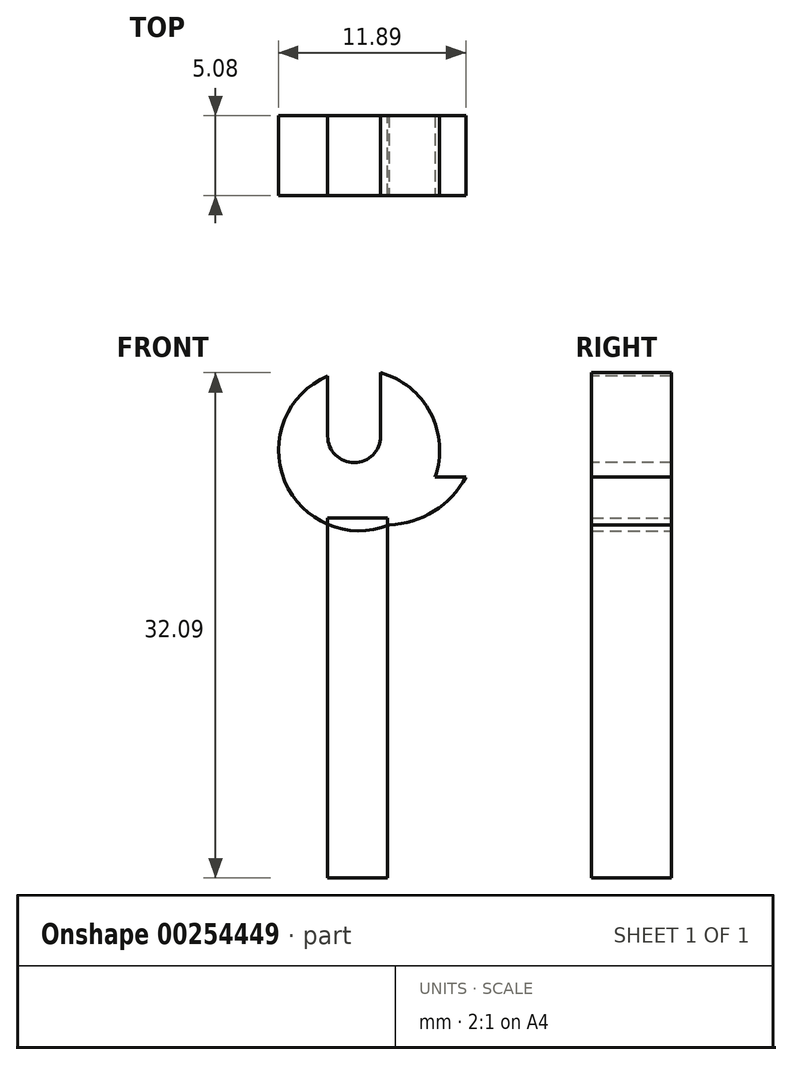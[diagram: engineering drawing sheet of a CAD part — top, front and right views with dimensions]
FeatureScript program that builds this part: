
annotation { "Feature Type Name" : "Feature", "Feature Type Description" : "" }
export const myFeature = defineFeature(function(context is Context, id is Id, definition is map)
    precondition{}
    {
        {
            var Q0;
            Q0=qCreatedBy(makeId("Front.planeOp"),FACE);
            var sketch = newSketch(context, id + "F0", { "sketchPlane" : qUnion([Q0])});
            skLineSegment(sketch, "E0.bottom", {"start": v(0, 0) * mm, "end": v(3.8, 0) * mm});
            skLineSegment(sketch, "E0.top", {"start": v(0, 22.86) * mm, "end": v(3.8, 22.86) * mm});
            skLineSegment(sketch, "E0.left", {"start": v(0, 0) * mm, "end": v(0, 22.86) * mm});
            skLineSegment(sketch, "E0.right", {"start": v(3.8, 0) * mm, "end": v(3.8, 22.86) * mm});
            skSolve(sketch);
        }
        {
            var Q0;
            Q0=qCreatedBy(makeId("Front.planeOp"),FACE);
            var sketch = newSketch(context, id + "F1", { "sketchPlane" : qUnion([Q0])});
            skCircle(sketch, "E1", {"center": v(2, 27.17) * mm, "radius": 5.11 * mm});
            skPoint(sketch, "E1.first.point", {"position": v(0, 22.46) * mm});
            skPoint(sketch, "E1.second.point", {"position": v(4, 22.46) * mm});
            skPoint(sketch, "E1.third.point", {"position": v(3.33, 32.1) * mm});
            skSolve(sketch);
        }
        {
            var Q0;
            Q0=makeQuery(id+"F1.imprint","IMPRINT",FACE,{"disambiguationData":[TD([[makeQuery(id+"F1.imprint","IMPRINT",EDGE,{"derivedFrom":sQuery(id+"F1.wireOp",EDGE,"E1")}),1.0]])]});
            var Q1;
            Q1=makeQuery(id+"F0.imprint","IMPRINT",FACE,{"disambiguationData":[TD([[makeQuery(id+"F0.imprint","IMPRINT",EDGE,{"derivedFrom":sQuery(id+"F0.wireOp",EDGE,"E0.bottom")}),1.0]])]});
            extrude(context, id + "F2", {"entities" : qUnion([Q0, Q1]), "depth" : 5.08 * mm});
        }
        {
            var Q0;
            Q0=makeQuery(id+"F2.opExtrude","CAP_FACE",FACE,{"disambiguationData":[OSD([sQuery(id+"F1.wireOp",EDGE,"E1")])],"isStart":false});
            var sketch = newSketch(context, id + "F3", { "sketchPlane" : qUnion([Q0])});
            skLineSegment(sketch, "E2", {"start": v(3.37, 32.1) * mm, "end": v(3.37, 28.06) * mm});
            skLineSegment(sketch, "E3", {"start": v(0, 31.87) * mm, "end": v(0, 28.06) * mm});
            skArc(sketch, "E4", {"start": v(0, 28.06) * mm, "mid": v(1.68, 26.37) * mm, "end": v(3.37, 28.06) * mm});
            skSolve(sketch);
        }
        {
            var Q0;
            {var subQ0=sQuery(id+"F3.wireOp",EDGE,"E2");Q0=makeQuery(id+"F3.imprint","IMPRINT",FACE,{"disambiguationData":[TD([[makeQuery(id+"F3.imprint","IMPRINT",EDGE,{"derivedFrom":subQ0}),-1.0]])]});}
            extrude(context, id + "F4", {"entities" : qUnion([Q0]), "operationType" : NewBodyOperationType.REMOVE, "endBound" : BoundingType.THROUGH_ALL, "oppositeDirection" : true, "depth" : 25.4 * mm});
        }
        {
            var Q0;
            Q0=makeQuery(id+"F2.opExtrude","CAP_FACE",FACE,{"disambiguationData":[OSD([sQuery(id+"F1.wireOp",EDGE,"E1")])],"isStart":false});
            var sketch = newSketch(context, id + "F5", { "sketchPlane" : qUnion([Q0])});
            skLineSegment(sketch, "E5", {"start": v(6.82, 25.47) * mm, "end": v(8.77, 25.47) * mm});
            skArc(sketch, "E6", {"start": v(3.9, 22.42) * mm, "mid": v(6.75, 23.3) * mm, "end": v(8.77, 25.47) * mm});
            skSolve(sketch);
        }
        {
            var Q0;
            {var subQ0=sQuery(id+"F5.wireOp",EDGE,"E5");Q0=makeQuery(id+"F5.imprint","IMPRINT",FACE,{"disambiguationData":[TD([[makeQuery(id+"F5.imprint","IMPRINT",EDGE,{"derivedFrom":subQ0}),-1.0]])]});}
            extrude(context, id + "F6", {"entities" : qUnion([Q0]), "operationType" : NewBodyOperationType.ADD, "oppositeDirection" : true, "depth" : 5.08 * mm});
        }
    });
